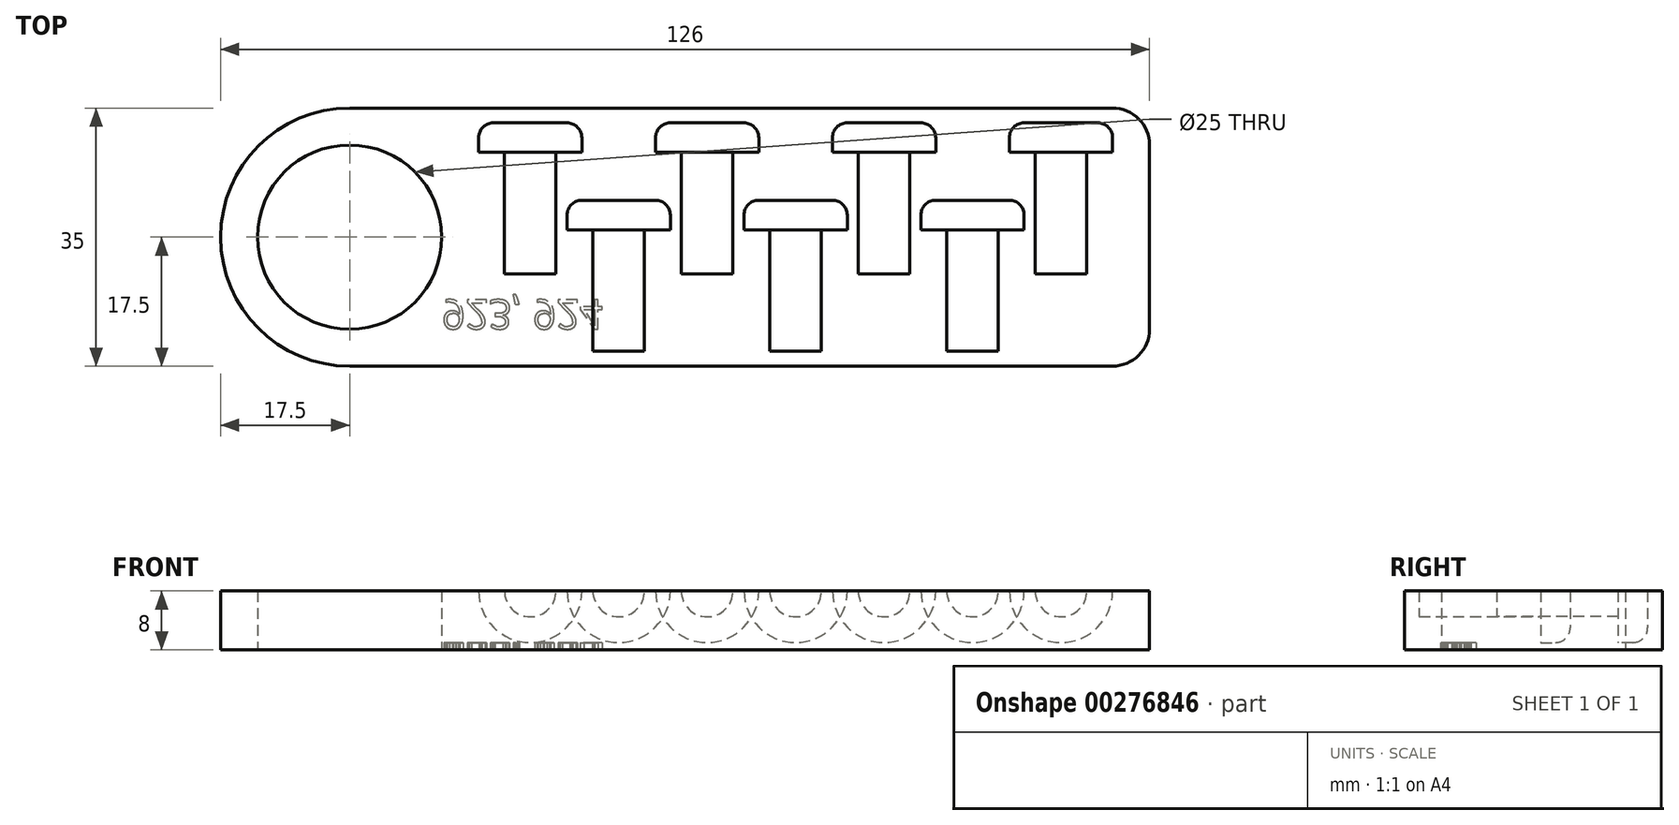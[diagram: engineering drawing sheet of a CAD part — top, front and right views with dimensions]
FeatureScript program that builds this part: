
annotation { "Feature Type Name" : "Feature", "Feature Type Description" : "" }
export const myFeature = defineFeature(function(context is Context, id is Id, definition is map)
    precondition{}
    {
        {
            var Q0;
            Q0=qCreatedBy(makeId("Top.planeOp"),FACE);
            var sketch = newSketch(context, id + "F0", { "sketchPlane" : qUnion([Q0])});
            skLineSegment(sketch, "E0.bottom", {"start": v(17.5, 0) * mm, "end": v(121, 0) * mm});
            skLineSegment(sketch, "E0.top", {"start": v(17.5, 35) * mm, "end": v(121, 35) * mm});
            skLineSegment(sketch, "E0.left", {"start": v(0, 17.5) * mm, "end": v(0, 17.5) * mm});
            skLineSegment(sketch, "E0.right", {"start": v(126, 5) * mm, "end": v(126, 30) * mm});
            skLineSegment(sketch, "E1.bottom", {"start": v(0, 0) * mm, "end": v(17.5, 0) * mm, "construction": true});
            skLineSegment(sketch, "E1.top", {"start": v(0, 17.5) * mm, "end": v(17.5, 17.5) * mm, "construction": true});
            skLineSegment(sketch, "E1.left", {"start": v(0, 0) * mm, "end": v(0, 17.5) * mm, "construction": true});
            skLineSegment(sketch, "E1.right", {"start": v(17.5, 0) * mm, "end": v(17.5, 17.5) * mm, "construction": true});
            skCircle(sketch, "E2", {"center": v(17.5, 17.5) * mm, "radius": 12.5 * mm});
            skPoint(sketch, "E3.visualSharp", {"position": v(0, 0) * mm});
            skArc(sketch, "E3.filletArc", {"start": v(0, 17.5) * mm, "mid": v(5.13, 5.13) * mm, "end": v(17.5, 0) * mm});
            skPoint(sketch, "E4.visualSharp", {"position": v(0, 35) * mm});
            skArc(sketch, "E4.filletArc", {"start": v(17.5, 35) * mm, "mid": v(5.13, 29.87) * mm, "end": v(0, 17.5) * mm});
            skPoint(sketch, "E5.visualSharp", {"position": v(126, 35) * mm});
            skArc(sketch, "E5.filletArc", {"start": v(126, 30) * mm, "mid": v(124.54, 33.54) * mm, "end": v(121, 35) * mm});
            skPoint(sketch, "E6.visualSharp", {"position": v(126, 0) * mm});
            skArc(sketch, "E6.filletArc", {"start": v(121, 0) * mm, "mid": v(124.54, 1.46) * mm, "end": v(126, 5) * mm});
            skSolve(sketch);
        }
        {
            var Q0;
            Q0=makeQuery(id+"F0.imprint","IMPRINT",FACE,{"disambiguationData":[TD([[makeQuery(id+"F0.imprint","IMPRINT",EDGE,{"derivedFrom":sQuery(id+"F0.wireOp",EDGE,"E0.bottom")}),1.0]])]});
            extrude(context, id + "F1", {"entities" : qUnion([Q0]), "depth" : 8 * mm});
        }
        {
            var Q0;
            Q0=makeQuery(id+"F1.opExtrude","CAP_FACE",FACE,{"disambiguationData":[OSD([sQuery(id+"F0.wireOp",EDGE,"E0.bottom"),sQuery(id+"F0.wireOp",EDGE,"E0.top"),sQuery(id+"F0.wireOp",EDGE,"E0.right"),sQuery(id+"F0.wireOp",EDGE,"E2"),sQuery(id+"F0.wireOp",EDGE,"E3.filletArc"),sQuery(id+"F0.wireOp",EDGE,"E4.filletArc"),sQuery(id+"F0.wireOp",EDGE,"E5.filletArc"),sQuery(id+"F0.wireOp",EDGE,"E6.filletArc")])],"isStart":false});
            var sketch = newSketch(context, id + "F2", { "sketchPlane" : qUnion([Q0])});
            skLineSegment(sketch, "E7.bottom", {"start": v(0, 0) * mm, "end": v(42, 0) * mm, "construction": true});
            skLineSegment(sketch, "E7.top", {"start": v(0, 33) * mm, "end": v(42, 33) * mm, "construction": true});
            skLineSegment(sketch, "E7.left", {"start": v(0, 0) * mm, "end": v(0, 33) * mm, "construction": true});
            skLineSegment(sketch, "E7.right", {"start": v(42, 0) * mm, "end": v(42, 33) * mm, "construction": true});
            skLineSegment(sketch, "E8.bottom", {"start": v(0, 0) * mm, "end": v(54, 0) * mm, "construction": true});
            skLineSegment(sketch, "E8.top", {"start": v(0, 2) * mm, "end": v(54, 2) * mm, "construction": true});
            skLineSegment(sketch, "E8.left", {"start": v(0, 0) * mm, "end": v(0, 2) * mm, "construction": true});
            skLineSegment(sketch, "E8.right", {"start": v(54, 0) * mm, "end": v(54, 2) * mm, "construction": true});
            skLineSegment(sketch, "E9", {"start": v(54, 2) * mm, "end": v(78, 2) * mm, "construction": true});
            skLineSegment(sketch, "E10", {"start": v(78, 2) * mm, "end": v(102, 2) * mm, "construction": true});
            skLineSegment(sketch, "E11.bottom", {"start": v(54, 2) * mm, "end": v(57.5, 2) * mm});
            skLineSegment(sketch, "E11.left", {"start": v(54, 2) * mm, "end": v(54, 18.5) * mm});
            skLineSegment(sketch, "E11.right", {"start": v(57.5, 2) * mm, "end": v(57.5, 18.5) * mm});
            skLineSegment(sketch, "E12.bottom", {"start": v(78, 2) * mm, "end": v(81.5, 2) * mm});
            skLineSegment(sketch, "E12.left", {"start": v(78, 2) * mm, "end": v(78, 18.5) * mm});
            skLineSegment(sketch, "E12.right", {"start": v(81.5, 2) * mm, "end": v(81.5, 18.5) * mm});
            skLineSegment(sketch, "E13.bottom", {"start": v(102, 2) * mm, "end": v(105.5, 2) * mm});
            skLineSegment(sketch, "E13.left", {"start": v(102, 2) * mm, "end": v(102, 18.5) * mm});
            skLineSegment(sketch, "E13.right", {"start": v(105.5, 2) * mm, "end": v(105.5, 18.5) * mm});
            skLineSegment(sketch, "E14.bottom", {"start": v(57.5, 18.5) * mm, "end": v(61, 18.5) * mm});
            skLineSegment(sketch, "E14.top", {"start": v(54, 22.5) * mm, "end": v(59, 22.5) * mm});
            skLineSegment(sketch, "E14.left", {"start": v(54, 18.5) * mm, "end": v(54, 22.5) * mm});
            skLineSegment(sketch, "E14.right", {"start": v(61, 18.5) * mm, "end": v(61, 20.5) * mm});
            skLineSegment(sketch, "E15.bottom", {"start": v(81.5, 18.5) * mm, "end": v(85, 18.5) * mm});
            skLineSegment(sketch, "E15.top", {"start": v(78, 22.5) * mm, "end": v(83, 22.5) * mm});
            skLineSegment(sketch, "E15.left", {"start": v(78, 18.5) * mm, "end": v(78, 22.5) * mm});
            skLineSegment(sketch, "E15.right", {"start": v(85, 18.5) * mm, "end": v(85, 20.5) * mm});
            skLineSegment(sketch, "E16.bottom", {"start": v(105.5, 18.5) * mm, "end": v(109, 18.5) * mm});
            skLineSegment(sketch, "E16.top", {"start": v(102, 22.5) * mm, "end": v(107, 22.5) * mm});
            skLineSegment(sketch, "E16.left", {"start": v(102, 18.5) * mm, "end": v(102, 22.5) * mm});
            skLineSegment(sketch, "E16.right", {"start": v(109, 18.5) * mm, "end": v(109, 20.5) * mm});
            skLineSegment(sketch, "E17.bottom", {"start": v(42, 33) * mm, "end": v(47, 33) * mm});
            skLineSegment(sketch, "E17.top", {"start": v(45.5, 29) * mm, "end": v(49, 29) * mm});
            skLineSegment(sketch, "E17.left", {"start": v(42, 33) * mm, "end": v(42, 29) * mm});
            skLineSegment(sketch, "E17.right", {"start": v(49, 31) * mm, "end": v(49, 29) * mm});
            skLineSegment(sketch, "E18.bottom", {"start": v(66, 33) * mm, "end": v(71, 33) * mm});
            skLineSegment(sketch, "E18.top", {"start": v(69.5, 29) * mm, "end": v(73, 29) * mm});
            skLineSegment(sketch, "E18.left", {"start": v(66, 33) * mm, "end": v(66, 29) * mm});
            skLineSegment(sketch, "E18.right", {"start": v(73, 31) * mm, "end": v(73, 29) * mm});
            skLineSegment(sketch, "E19.bottom", {"start": v(90, 33) * mm, "end": v(95, 33) * mm});
            skLineSegment(sketch, "E19.top", {"start": v(93.5, 29) * mm, "end": v(97, 29) * mm});
            skLineSegment(sketch, "E19.left", {"start": v(90, 33) * mm, "end": v(90, 29) * mm});
            skLineSegment(sketch, "E19.right", {"start": v(97, 31) * mm, "end": v(97, 29) * mm});
            skLineSegment(sketch, "E20.bottom", {"start": v(114, 33) * mm, "end": v(119, 33) * mm});
            skLineSegment(sketch, "E20.top", {"start": v(117.5, 29) * mm, "end": v(121, 29) * mm});
            skLineSegment(sketch, "E20.left", {"start": v(114, 33) * mm, "end": v(114, 29) * mm});
            skLineSegment(sketch, "E20.right", {"start": v(121, 31) * mm, "end": v(121, 29) * mm});
            skLineSegment(sketch, "E21.top", {"start": v(42, 12.5) * mm, "end": v(45.5, 12.5) * mm});
            skLineSegment(sketch, "E21.left", {"start": v(42, 29) * mm, "end": v(42, 12.5) * mm});
            skLineSegment(sketch, "E21.right", {"start": v(45.5, 29) * mm, "end": v(45.5, 12.5) * mm});
            skLineSegment(sketch, "E22.top", {"start": v(66, 12.5) * mm, "end": v(69.5, 12.5) * mm});
            skLineSegment(sketch, "E22.left", {"start": v(66, 29) * mm, "end": v(66, 12.5) * mm});
            skLineSegment(sketch, "E22.right", {"start": v(69.5, 29) * mm, "end": v(69.5, 12.5) * mm});
            skLineSegment(sketch, "E23.top", {"start": v(90, 12.5) * mm, "end": v(93.5, 12.5) * mm});
            skLineSegment(sketch, "E23.left", {"start": v(90, 29) * mm, "end": v(90, 12.5) * mm});
            skLineSegment(sketch, "E23.right", {"start": v(93.5, 29) * mm, "end": v(93.5, 12.5) * mm});
            skLineSegment(sketch, "E24.top", {"start": v(114, 12.5) * mm, "end": v(117.5, 12.5) * mm});
            skLineSegment(sketch, "E24.left", {"start": v(114, 29) * mm, "end": v(114, 12.5) * mm});
            skLineSegment(sketch, "E24.right", {"start": v(117.5, 29) * mm, "end": v(117.5, 12.5) * mm});
            skPoint(sketch, "E25.visualSharp", {"position": v(49, 33) * mm});
            skArc(sketch, "E25.filletArc", {"start": v(49, 31) * mm, "mid": v(48.41, 32.41) * mm, "end": v(47, 33) * mm});
            skLineSegment(sketch, "E26", {"start": v(42, 12.5) * mm, "end": v(66, 12.5) * mm, "construction": true});
            skLineSegment(sketch, "E27", {"start": v(66, 12.5) * mm, "end": v(90, 12.5) * mm, "construction": true});
            skLineSegment(sketch, "E28", {"start": v(90, 12.5) * mm, "end": v(114, 12.5) * mm, "construction": true});
            skPoint(sketch, "E29.visualSharp", {"position": v(61, 22.5) * mm});
            skArc(sketch, "E29.filletArc", {"start": v(61, 20.5) * mm, "mid": v(60.41, 21.91) * mm, "end": v(59, 22.5) * mm});
            skPoint(sketch, "E30.visualSharp", {"position": v(85, 22.5) * mm});
            skArc(sketch, "E30.filletArc", {"start": v(85, 20.5) * mm, "mid": v(84.41, 21.91) * mm, "end": v(83, 22.5) * mm});
            skPoint(sketch, "E31.visualSharp", {"position": v(109, 22.5) * mm});
            skArc(sketch, "E31.filletArc", {"start": v(109, 20.5) * mm, "mid": v(108.41, 21.91) * mm, "end": v(107, 22.5) * mm});
            skPoint(sketch, "E32.visualSharp", {"position": v(121, 33) * mm});
            skArc(sketch, "E32.filletArc", {"start": v(121, 31) * mm, "mid": v(120.41, 32.41) * mm, "end": v(119, 33) * mm});
            skPoint(sketch, "E33.visualSharp", {"position": v(97, 33) * mm});
            skArc(sketch, "E33.filletArc", {"start": v(97, 31) * mm, "mid": v(96.41, 32.41) * mm, "end": v(95, 33) * mm});
            skPoint(sketch, "E34.visualSharp", {"position": v(73, 33) * mm});
            skArc(sketch, "E34.filletArc", {"start": v(73, 31) * mm, "mid": v(72.41, 32.41) * mm, "end": v(71, 33) * mm});
            skSolve(sketch);
        }
        {
            var Q0;
            Q0=makeQuery(id+"F2.imprint","IMPRINT",FACE,{"disambiguationData":[TD([[makeQuery(id+"F2.imprint","IMPRINT",EDGE,{"derivedFrom":sQuery(id+"F2.wireOp",EDGE,"E17.bottom")}),-1.0]])]});
            var Q1;
            Q1=sQuery(id+"F2.wireOp",EDGE,"E21.left");
            revolve(context, id + "F3", {"operationType" : NewBodyOperationType.REMOVE, "entities" : qUnion([Q0]), "axis" : qUnion([Q1]), "revolveType" : RevolveType.FULL, "oppositeDirection" : true});
        }
        {
            var Q0;
            Q0=makeQuery(id+"F2.imprint","IMPRINT",FACE,{"disambiguationData":[TD([[makeQuery(id+"F2.imprint","IMPRINT",EDGE,{"derivedFrom":sQuery(id+"F2.wireOp",EDGE,"E11.bottom")}),1.0]])]});
            var Q1;
            Q1=sQuery(id+"F2.wireOp",EDGE,"E11.left");
            revolve(context, id + "F4", {"operationType" : NewBodyOperationType.REMOVE, "entities" : qUnion([Q0]), "axis" : qUnion([Q1]), "revolveType" : RevolveType.FULL, "oppositeDirection" : true});
        }
        {
            var Q0;
            Q0=makeQuery(id+"F2.imprint","IMPRINT",FACE,{"disambiguationData":[TD([[makeQuery(id+"F2.imprint","IMPRINT",EDGE,{"derivedFrom":sQuery(id+"F2.wireOp",EDGE,"E18.bottom")}),-1.0]])]});
            var Q1;
            Q1=sQuery(id+"F2.wireOp",EDGE,"E22.left");
            revolve(context, id + "F5", {"operationType" : NewBodyOperationType.REMOVE, "entities" : qUnion([Q0]), "axis" : qUnion([Q1]), "revolveType" : RevolveType.FULL, "oppositeDirection" : true});
        }
        {
            var Q0;
            Q0=makeQuery(id+"F2.imprint","IMPRINT",FACE,{"disambiguationData":[TD([[makeQuery(id+"F2.imprint","IMPRINT",EDGE,{"derivedFrom":sQuery(id+"F2.wireOp",EDGE,"E12.bottom")}),1.0]])]});
            var Q1;
            Q1=sQuery(id+"F2.wireOp",EDGE,"E12.left");
            revolve(context, id + "F6", {"operationType" : NewBodyOperationType.REMOVE, "entities" : qUnion([Q0]), "axis" : qUnion([Q1]), "revolveType" : RevolveType.FULL, "oppositeDirection" : true});
        }
        {
            var Q0;
            Q0=makeQuery(id+"F2.imprint","IMPRINT",FACE,{"disambiguationData":[TD([[makeQuery(id+"F2.imprint","IMPRINT",EDGE,{"derivedFrom":sQuery(id+"F2.wireOp",EDGE,"E13.bottom")}),1.0]])]});
            var Q1;
            Q1=sQuery(id+"F2.wireOp",EDGE,"E13.left");
            revolve(context, id + "F7", {"operationType" : NewBodyOperationType.REMOVE, "entities" : qUnion([Q0]), "axis" : qUnion([Q1]), "revolveType" : RevolveType.FULL, "oppositeDirection" : true});
        }
        {
            var Q0;
            Q0=makeQuery(id+"F2.imprint","IMPRINT",FACE,{"disambiguationData":[TD([[makeQuery(id+"F2.imprint","IMPRINT",EDGE,{"derivedFrom":sQuery(id+"F2.wireOp",EDGE,"E19.bottom")}),-1.0]])]});
            var Q1;
            Q1=sQuery(id+"F2.wireOp",EDGE,"E23.left");
            revolve(context, id + "F8", {"operationType" : NewBodyOperationType.REMOVE, "entities" : qUnion([Q0]), "axis" : qUnion([Q1]), "revolveType" : RevolveType.FULL, "oppositeDirection" : true});
        }
        {
            var Q0;
            Q0=makeQuery(id+"F2.imprint","IMPRINT",FACE,{"disambiguationData":[TD([[makeQuery(id+"F2.imprint","IMPRINT",EDGE,{"derivedFrom":sQuery(id+"F2.wireOp",EDGE,"E20.bottom")}),-1.0]])]});
            var Q1;
            Q1=sQuery(id+"F2.wireOp",EDGE,"E24.left");
            revolve(context, id + "F9", {"operationType" : NewBodyOperationType.REMOVE, "entities" : qUnion([Q0]), "axis" : qUnion([Q1]), "revolveType" : RevolveType.FULL, "oppositeDirection" : true});
        }
        {
            var Q0;
            Q0=makeQuery(id+"F1.opExtrude","CAP_FACE",FACE,{"disambiguationData":[OSD([sQuery(id+"F0.wireOp",EDGE,"E0.bottom"),sQuery(id+"F0.wireOp",EDGE,"E0.top"),sQuery(id+"F0.wireOp",EDGE,"E0.right"),sQuery(id+"F0.wireOp",EDGE,"E2"),sQuery(id+"F0.wireOp",EDGE,"E3.filletArc"),sQuery(id+"F0.wireOp",EDGE,"E4.filletArc"),sQuery(id+"F0.wireOp",EDGE,"E5.filletArc"),sQuery(id+"F0.wireOp",EDGE,"E6.filletArc")])],"isStart":true});
            var sketch = newSketch(context, id + "F10", { "sketchPlane" : qUnion([Q0])});
            skLineSegment(sketch, "E35.bottom", {"start": v(0, 0) * mm, "end": v(30, 0) * mm, "construction": true});
            skLineSegment(sketch, "E35.top", {"start": v(0, -5) * mm, "end": v(30, -5) * mm, "construction": true});
            skLineSegment(sketch, "E35.left", {"start": v(0, 0) * mm, "end": v(0, -5) * mm, "construction": true});
            skLineSegment(sketch, "E35.right", {"start": v(30, 0) * mm, "end": v(30, -5) * mm, "construction": true});
            skText(sketch, "E36", { "text": "923, 924", "fontName": "OpenSans-Regular.ttf"});
            const initialGuessF10  = {"E36": [0.03, -0.009, 1, 0, 0.004]};
            skSetInitialGuess(sketch, initialGuessF10);
            skSolve(sketch);
        }
        {
            var Q0;
            Q0 = qSketchRegion(id + "F10", true);
            extrude(context, id + "F11", {"entities" : qUnion([Q0]), "operationType" : NewBodyOperationType.REMOVE, "oppositeDirection" : true, "depth" : 1 * mm});
        }
    });
